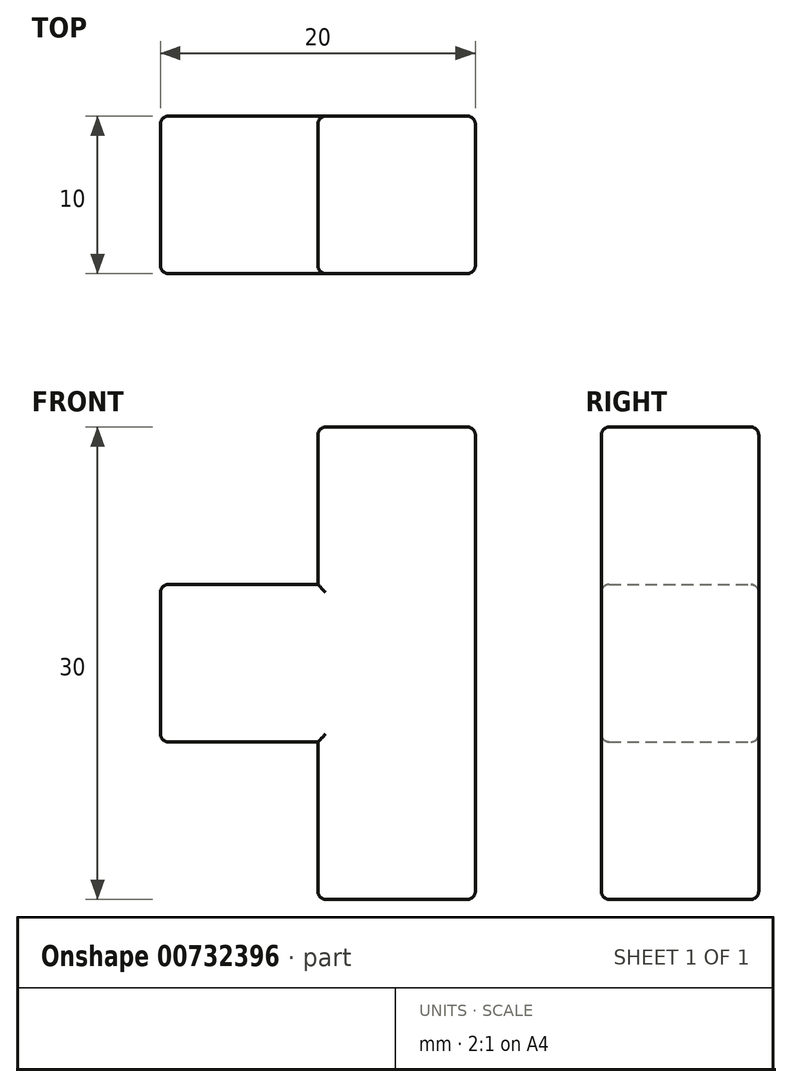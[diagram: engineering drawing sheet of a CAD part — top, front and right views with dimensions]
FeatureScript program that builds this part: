
annotation { "Feature Type Name" : "Feature", "Feature Type Description" : "" }
export const myFeature = defineFeature(function(context is Context, id is Id, definition is map)
    precondition{}
    {
        {
            var Q0;
            Q0=qCreatedBy(makeId("Front.planeOp"),FACE);
            var sketch = newSketch(context, id + "F0", { "sketchPlane" : qUnion([Q0])});
            skLineSegment(sketch, "E0.bottom", {"start": v(5, 15) * mm, "end": v(-5, 15) * mm});
            skLineSegment(sketch, "E0.top", {"start": v(5, -15) * mm, "end": v(-5, -15) * mm});
            skLineSegment(sketch, "E0.left", {"start": v(5, 15) * mm, "end": v(5, -15) * mm});
            skLineSegment(sketch, "E0.right", {"start": v(-5, 15) * mm, "end": v(-5, -15) * mm});
            skPoint(sketch, "E0.middle", {"position": v(0, 0) * mm});
            skLineSegment(sketch, "E1", {"start": v(-5, -5) * mm, "end": v(-15, -5) * mm});
            skLineSegment(sketch, "E2", {"start": v(-15, -5) * mm, "end": v(-15, 5) * mm});
            skLineSegment(sketch, "E3", {"start": v(-15, 5) * mm, "end": v(-5, 5) * mm});
            skSolve(sketch);
        }
        {
            var Q0;
            Q0 = qSketchRegion(id + "F0", true);
            extrude(context, id + "F1", {"entities" : qUnion([Q0]), "depth" : 10 * mm, "offsetDistance" : 25 * mm});
        }
        {
            var Q0;
            Q0=makeQuery(id+"F1.opExtrude","CAP_FACE",FACE,{"disambiguationData":[OSD([sQuery(id+"F0.wireOp",EDGE,"E0.bottom"),sQuery(id+"F0.wireOp",EDGE,"E0.top"),sQuery(id+"F0.wireOp",EDGE,"E0.left"),sQuery(id+"F0.wireOp",EDGE,"E0.right"),sQuery(id+"F0.wireOp",EDGE,"E1"),sQuery(id+"F0.wireOp",EDGE,"E2"),sQuery(id+"F0.wireOp",EDGE,"E3")])],"isStart":false});
            var Q1;
            Q1=makeQuery(id+"F1.opExtrude","CAP_FACE",FACE,{"disambiguationData":[OSD([sQuery(id+"F0.wireOp",EDGE,"E0.bottom"),sQuery(id+"F0.wireOp",EDGE,"E0.top"),sQuery(id+"F0.wireOp",EDGE,"E0.left"),sQuery(id+"F0.wireOp",EDGE,"E0.right"),sQuery(id+"F0.wireOp",EDGE,"E1"),sQuery(id+"F0.wireOp",EDGE,"E2"),sQuery(id+"F0.wireOp",EDGE,"E3")])],"isStart":true});
            var Q2;
            Q2=makeQuery(id+"F1.opExtrude","SWEPT_FACE",FACE,{"disambiguationData":[OSD([sQuery(id+"F0.wireOp",EDGE,"E0.bottom")])]});
            var Q3;
            Q3=makeQuery(id+"F1.opExtrude","SWEPT_FACE",FACE,{"disambiguationData":[OSD([sQuery(id+"F0.wireOp",EDGE,"E2")])]});
            var Q4;
            Q4=makeQuery(id+"F1.opExtrude","SWEPT_FACE",FACE,{"disambiguationData":[OSD([sQuery(id+"F0.wireOp",EDGE,"E0.top")])]});
            fillet(context, id + "F2", {"entities" : qUnion([Q0, Q1, Q2, Q3, Q4]), "radius" : 0.5 * mm, "tangentPropagation" : true, "allowEdgeOverflow" : false});
        }
    });
